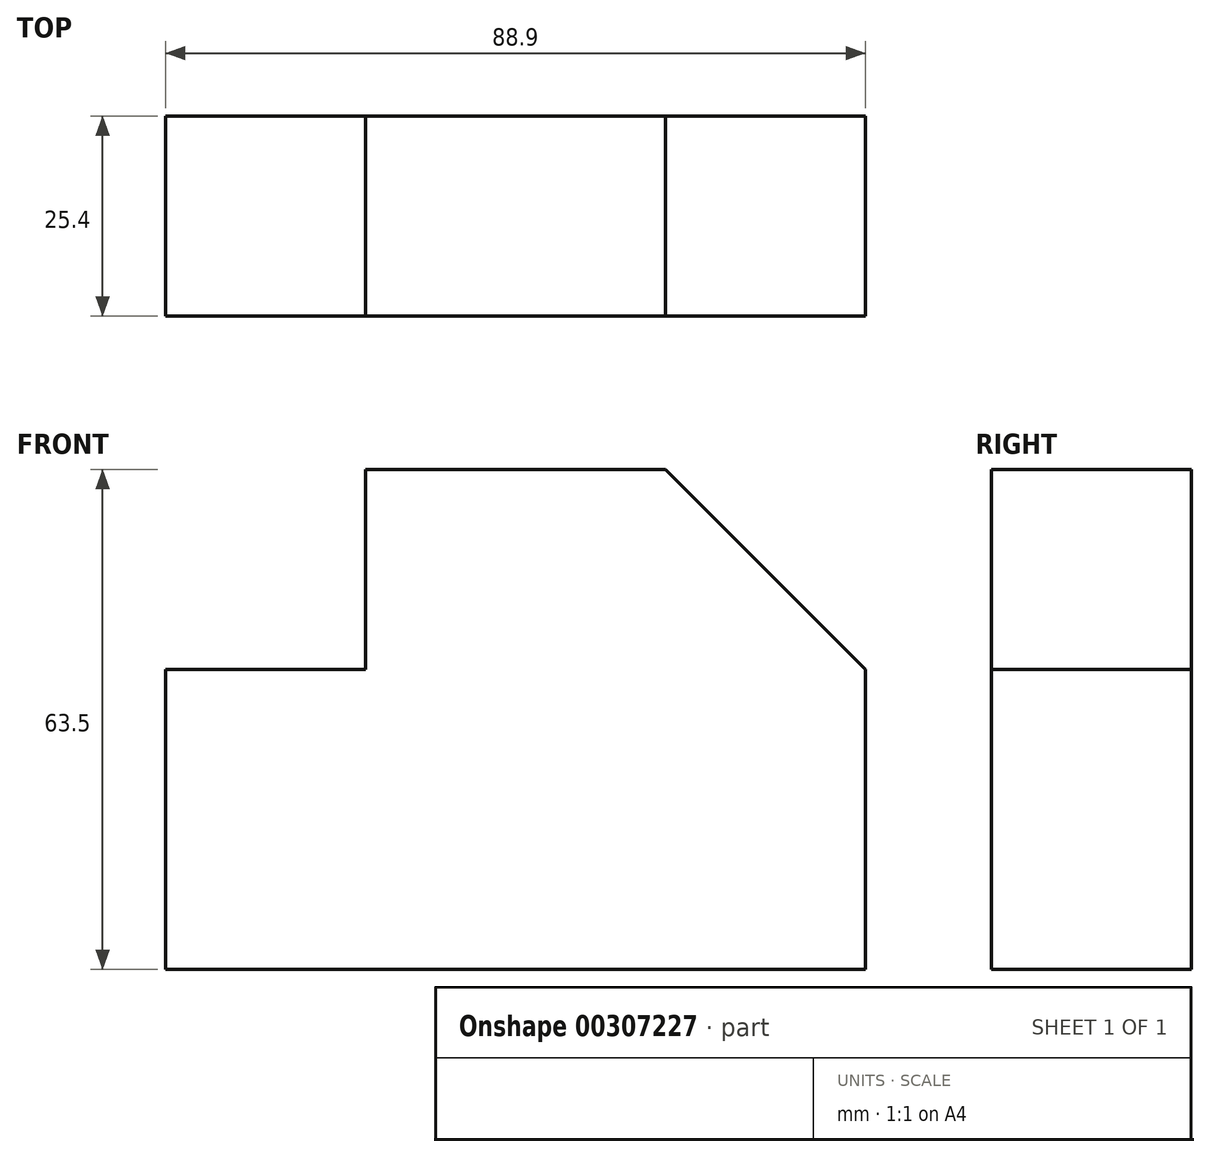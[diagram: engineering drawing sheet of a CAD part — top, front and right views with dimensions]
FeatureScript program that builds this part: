
annotation { "Feature Type Name" : "Feature", "Feature Type Description" : "" }
export const myFeature = defineFeature(function(context is Context, id is Id, definition is map)
    precondition{}
    {
        {
            var Q0;
            Q0=qCreatedBy(makeId("Front.planeOp"),FACE);
            var sketch = newSketch(context, id + "F0", { "sketchPlane" : qUnion([Q0])});
            skLineSegment(sketch, "E0", {"start": v(-64.8, -63.33) * mm, "end": v(24.1, -63.33) * mm});
            skLineSegment(sketch, "E1", {"start": v(24.1, -63.33) * mm, "end": v(24.1, -25.23) * mm});
            skLineSegment(sketch, "E2", {"start": v(24.1, -25.23) * mm, "end": v(-1.3, 0.17) * mm});
            skLineSegment(sketch, "E3", {"start": v(-1.3, 0.17) * mm, "end": v(-39.4, 0.17) * mm});
            skLineSegment(sketch, "E4", {"start": v(-39.4, 0.17) * mm, "end": v(-39.4, -25.23) * mm});
            skLineSegment(sketch, "E5", {"start": v(-39.4, -25.23) * mm, "end": v(-64.8, -25.23) * mm});
            skLineSegment(sketch, "E6", {"start": v(-64.8, -25.23) * mm, "end": v(-64.8, -63.33) * mm});
            skSolve(sketch);
        }
        {
            var Q0;
            Q0=makeQuery(id+"F0.imprint","IMPRINT",FACE,{"disambiguationData":[TD([[makeQuery(id+"F0.imprint","IMPRINT",EDGE,{"derivedFrom":sQuery(id+"F0.wireOp",EDGE,"E0")}),1.0]])]});
            extrude(context, id + "F1", {"entities" : qUnion([Q0]), "depth" : 25.4 * mm});
        }
    });
